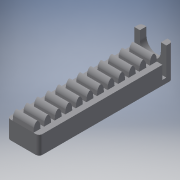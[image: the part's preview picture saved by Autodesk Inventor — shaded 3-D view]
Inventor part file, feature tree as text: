
AUTODESK INVENTOR PART (.ipt)
format: ipt  version: 2018 (Build 220112000, 112)  size: 386,048 bytes
history: native  units: in
note: dims shown in document units (in); Inventor stores cm internally (conversion verified against a paired STEP export)
features: extrude x8, sketch x8, other x7, reference x4, projected_geometry x3, fillet x1
ambient origin geometry x8: Origin, YZ Plane, XZ Plane, XY Plane, X Axis, Y Axis, Z Axis, Center Point
bodies: Body1 (feature_tree)
feature tree (31):
  extrude  "Extrusion2"  Depth=0.435in
  sketch  "Sketch3"  dims[d6=0.385in d7=0.0in d9=0.092in]
  extrude  "Extrusion6"  Depth=0.385in
  extrude  "Extrusion8"  Depth=0.1in
  extrude  "Extrusion16"  Depth=0.3937in
  extrude  "Extrusion17"  Depth=0.25in TaperAngle=0.0deg
  extrude  "Extrusion18"  Depth=0.0472in TaperAngle=0.0deg
  extrude  "Extrusion19"  Depth=0.3937in
  fillet  "Fillet2"  Radius=0.3937in
  extrude  "Extrusion20"  Depth=0.0787in TaperAngle=0.0deg
  sketch  "Sketch2"  dims[d4=2.5in d5=0.435in]
  sketch  "Sketch5"  dims[d58=0.1in d59=0.0in d63=0.5814in]
  projected_geometry  "Projected Loop1"
  projected_geometry  "Projected Loop2"
  projected_geometry  "Projected Loop3"
  sketch  "Sketch14"  dims[d64=0.5814in d72=7.874in d74=0.1271in d75=0.3937in d77=1.0in]
  sketch  "Sketch15"  dims[d79=0.25in d80=0.0in d106=1.0in d107=0.0in]
  sketch  "Sketch16"  dims[d108=0.0591in d109=0.0472in d110=0.0in]
  reference  "Reference1"
  sketch  "Sketch17"  dims[d111=0.1177in d112=0.1177in d113=0.3937in]
  reference  "Reference2"
  sketch  "Sketch18"  dims[d114=0.3937in d115=0.0787in d116=0.0in d117=1.0in d118=0.0in d119=0.0394in d120=1.0in d121=0.0in]
  reference  "Reference3"
  reference  "Reference4"
  other  "<userpath>\OneDrive\Documents\Inventor\TSA\2018\Animatronics\Tortoise\TurtleAssembly2.iam"
  other  "TurtleAssembly2.iam"
  other  "SyringEnd:5"
  other  "SyringEnd:4"
  other  "Glyptodon.iam"
  other  "wheelframe:1"
  other  "Frame:1"
